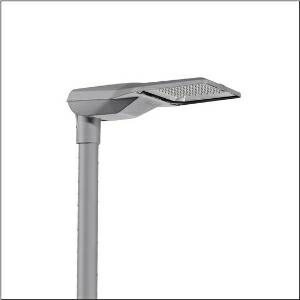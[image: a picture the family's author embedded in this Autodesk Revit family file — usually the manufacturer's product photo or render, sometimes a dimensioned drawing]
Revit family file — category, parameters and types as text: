
# Revit family: streetlight_sl_21_iq_midi___pl52_5xe3h31g08mb_961f
name_source: partatom
category: Lighting Fixtures
units: mm (PartAtom-declared; Revit-internal decimal feet)

## family parameters
Cut with Voids When Loaded = No
Host = Face
Light Source = No
Part Type = Normal
Room Calculation Point = No
Round Connector Dimension = Use Diameter
Shared = No

## types (1)
- --- (1 x LED, 19170 lm, 146.7 W, 3000K)
    Apparent Load = 147 VA
    CIE Flux Codes = 27 59 98 100 100
    Color Rendering = 70
    Color Temperature = 3000K
    Default Elevation = 1800 mm
    Description = Streetlight SL 21 iQ midi, mast luminaire, primary light control with lens, of PMMA, primary optical cover: cover, of toughened safety glass, transparent, light distribution: PL52, light emission: direct distribution, primary light characteristic: asymmetric, installation type: post-top, side-entry, LED, High Power LED, rated luminous flux: 19.170lm, luminous efficacy: 131lm/W, light colour: 730, colour temperature: 3000K, control gear: iQ Street-Remote, control: Street-Remote, Auto-Match, Temp-Guard, Lumen-Switch, Night-Set, Smart-Wire, Light-Fading, Desk-Remote (wireless, voltage-free reading and setting of iQ features in the workshop via application-optimized NFC function/RFID function), optimised constant luminous flux control (CLO 2.0), pre-setting: linear dimming characteristic, mains connection: 230..240V, AC, 50/60Hz, start of lifetime: 147W, end of service life: 161W, reduction: 62W, luminaire housing, of diecast aluminium, powder-coated, SITECO metallic grey (DB 702S), corrosivity category C5 high according to DIN EN ISO 12944, please order mast flange separately, inclination adjustable: 0°, 5°, 10°, 15°, sealing non-destructively replaceable, multi-level sealing system, length: 644mm, width: 335mm, height: 110mm, mast flange for spigot size: 42mm (side-entry): 5XC10008XM4, 60/48mm (side-entry/post-top): 5XC10108XM2, 76/60mm (side-entry/post-top): 5XC10108XM1, mounting height: 4..8m, protection rating (complete): IP66, insulation class (complete): insulation class II (safety insulation), certification: CE, ENEC, ENEC+, VDE, impact resistance: IK10, permissible operating ambient temperature for outdoor applications: -40..+50°C, standard-compliant lighting for roads and squares, packaging unit: 1 piece

Light Distribution: PL52
    Height = 111 mm
    Lamp = 1 x LED
    Lamp Light Flux = 19170 lm
    Lamp Power = 146.7 W
    Lamp count = 1
    Length = 644 mm
    Luminous efficacy = 131 lm/W
    Manufacturer = Siteco
    ModVariant = No
    Model = 5XE3H31G08MB
    Number of Poles = 1
    OnlyDefault = Yes
    Power Factor = 1
    Product Name = Streetlight SL 21 iQ midi | PL52
    Product group = mast luminaire | pylon top
    ProductGroupID = 6100
    Protection Class = Protection class II
    Protection Degree = IP 66
    RLX_Detail_Level = 1
    RLX_Emergency_Light_Flux = 0 lm
    RLX_Emergency_Type = 0
    RLX_Emergency_Type_DB = No
    RlxData = <blob elided: 36505 chars, md5=2aedc255>
    Socket = socket
    Standby Power = 0 W
    System Light Flux = 19169 lm
    System Power = 147 W
    Type Comments = factory setting: luminous flux: 100 % | dim-lin: 254 | 753 mA
    Type Image = l_1004298.jpg
    URL = http://relux.com
    VarID = @adj_188243
    Voltage = 0 V
    Weight = 0.00 kg
    Width = 336 mm

## geometry (parser evidence)
native form markers: Blend x4, Sweep x10
no freeform markers — native parametric forms only
